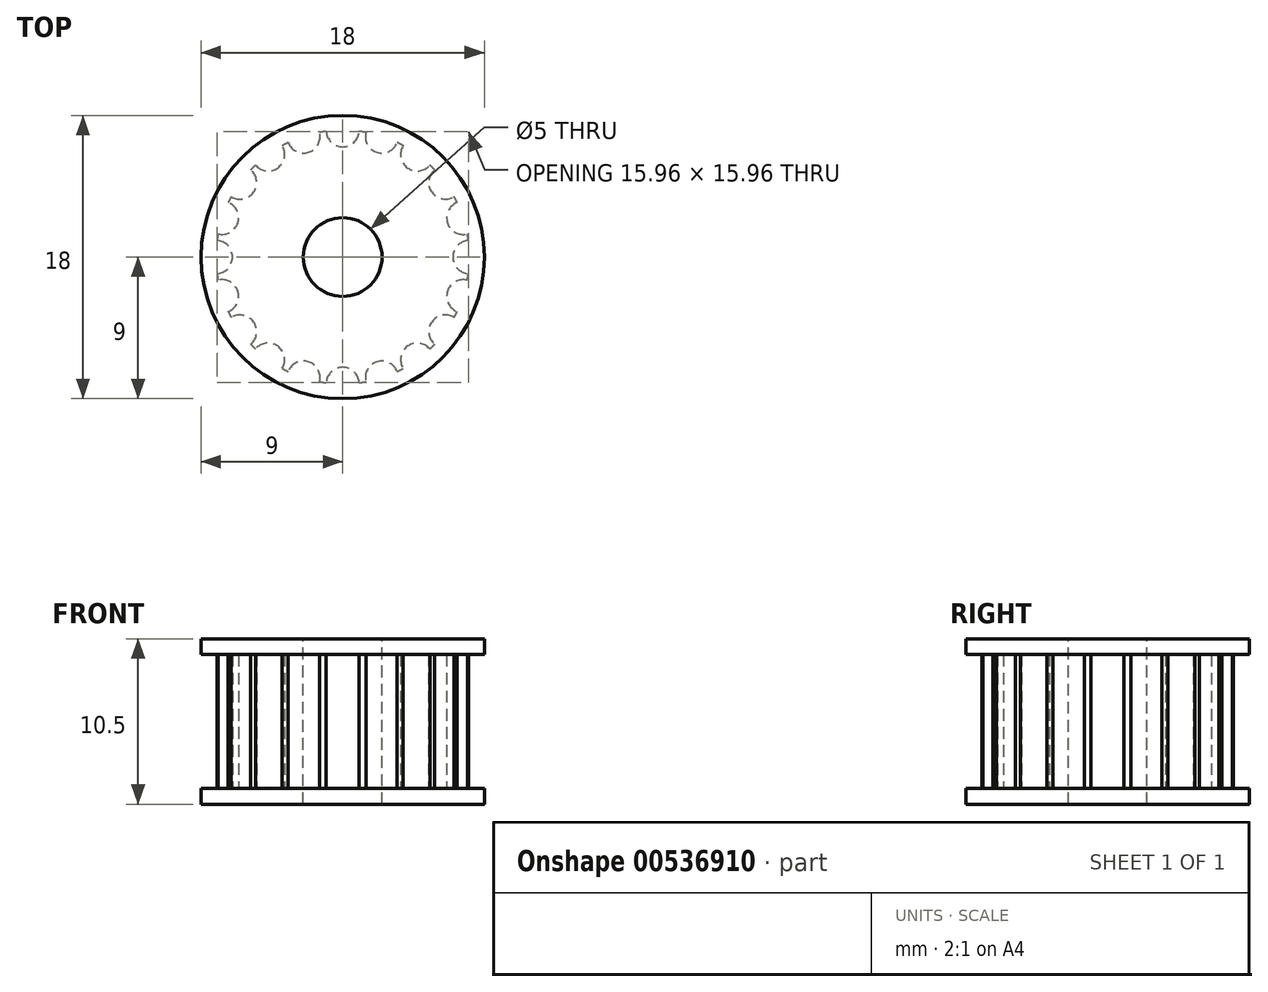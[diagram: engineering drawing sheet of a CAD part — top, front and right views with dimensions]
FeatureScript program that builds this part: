
annotation { "Feature Type Name" : "Feature", "Feature Type Description" : "" }
export const myFeature = defineFeature(function(context is Context, id is Id, definition is map)
    precondition{}
    {
        {
            var Q0;
            Q0=qCreatedBy(makeId("Front.planeOp"),FACE);
            var sketch = newSketch(context, id + "F0", { "sketchPlane" : qUnion([Q0])});
            skLineSegment(sketch, "E0", {"start": v(0, 14.86) * mm, "end": v(0, -20.88) * mm, "construction": true});
            skLineSegment(sketch, "E1", {"start": v(2.5, 5.25) * mm, "end": v(9, 5.25) * mm});
            skLineSegment(sketch, "E2", {"start": v(9, 5.25) * mm, "end": v(9, 4.25) * mm});
            skLineSegment(sketch, "E3", {"start": v(9, 4.25) * mm, "end": v(7, 4.25) * mm});
            skLineSegment(sketch, "E4", {"start": v(7, 4.25) * mm, "end": v(7, -4.25) * mm});
            skLineSegment(sketch, "E5", {"start": v(7, -4.25) * mm, "end": v(9, -4.25) * mm});
            skLineSegment(sketch, "E6", {"start": v(9, -4.25) * mm, "end": v(9, -5.25) * mm});
            skLineSegment(sketch, "E7", {"start": v(9, -5.25) * mm, "end": v(2.5, -5.25) * mm});
            skLineSegment(sketch, "E8", {"start": v(2.5, 5.25) * mm, "end": v(2.5, -5.25) * mm});
            skLineSegment(sketch, "E9", {"start": v(0, 0) * mm, "end": v(2.5, 0) * mm, "construction": true});
            skSolve(sketch);
        }
        {
            var Q0;
            Q0=makeQuery(id+"F0.imprint","IMPRINT",FACE,{"disambiguationData":[TD([[makeQuery(id+"F0.imprint","IMPRINT",EDGE,{"derivedFrom":sQuery(id+"F0.wireOp",EDGE,"E1")}),-1.0]])]});
            var Q1;
            Q1=sQuery(id+"F0.wireOp",EDGE,"E0");
            revolve(context, id + "F1", {"entities" : qUnion([Q0]), "axis" : qUnion([Q1]), "revolveType" : RevolveType.FULL});
        }
        {
            var Q0;
            Q0=makeQuery(id+"F1.opRevolve","SWEPT_FACE",FACE,{"disambiguationData":[OSD([sQuery(id+"F0.wireOp",EDGE,"E5")])]});
            var sketch = newSketch(context, id + "F2", { "sketchPlane" : qUnion([Q0])});
            skArc(sketch, "E10", {"start": v(-1.05, 7.98) * mm, "mid": v(0, 7) * mm, "end": v(1.05, 7.98) * mm});
            skArc(sketch, "E11.1.0", {"start": v(-3.46, 7.27) * mm, "mid": v(-2.16, 6.66) * mm, "end": v(-1.47, 7.91) * mm});
            skArc(sketch, "E11.2.0", {"start": v(-5.54, 5.84) * mm, "mid": v(-4.11, 5.66) * mm, "end": v(-3.84, 7.07) * mm});
            skArc(sketch, "E11.3.0", {"start": v(-7.07, 3.84) * mm, "mid": v(-5.66, 4.11) * mm, "end": v(-5.84, 5.54) * mm});
            skArc(sketch, "E11.4.0", {"start": v(-7.91, 1.47) * mm, "mid": v(-6.66, 2.16) * mm, "end": v(-7.27, 3.46) * mm});
            skArc(sketch, "E11.5.0", {"start": v(-7.98, -1.05) * mm, "mid": v(-7, 0) * mm, "end": v(-7.98, 1.05) * mm});
            skArc(sketch, "E11.6.0", {"start": v(-7.27, -3.46) * mm, "mid": v(-6.66, -2.16) * mm, "end": v(-7.91, -1.47) * mm});
            skArc(sketch, "E11.7.0", {"start": v(-5.84, -5.54) * mm, "mid": v(-5.66, -4.11) * mm, "end": v(-7.07, -3.84) * mm});
            skArc(sketch, "E11.8.0", {"start": v(-3.84, -7.07) * mm, "mid": v(-4.11, -5.66) * mm, "end": v(-5.54, -5.84) * mm});
            skArc(sketch, "E11.9.0", {"start": v(-1.47, -7.91) * mm, "mid": v(-2.16, -6.66) * mm, "end": v(-3.46, -7.27) * mm});
            skArc(sketch, "E11.10.0", {"start": v(1.05, -7.98) * mm, "mid": v(0, -7) * mm, "end": v(-1.05, -7.98) * mm});
            skArc(sketch, "E11.11.0", {"start": v(3.46, -7.27) * mm, "mid": v(2.16, -6.66) * mm, "end": v(1.47, -7.91) * mm});
            skArc(sketch, "E11.12.0", {"start": v(5.54, -5.84) * mm, "mid": v(4.11, -5.66) * mm, "end": v(3.84, -7.07) * mm});
            skArc(sketch, "E11.13.0", {"start": v(7.07, -3.84) * mm, "mid": v(5.66, -4.11) * mm, "end": v(5.84, -5.54) * mm});
            skArc(sketch, "E11.14.0", {"start": v(7.91, -1.47) * mm, "mid": v(6.66, -2.16) * mm, "end": v(7.27, -3.46) * mm});
            skArc(sketch, "E11.15.0", {"start": v(7.98, 1.05) * mm, "mid": v(7, 0) * mm, "end": v(7.98, -1.05) * mm});
            skArc(sketch, "E11.16.0", {"start": v(7.27, 3.46) * mm, "mid": v(6.66, 2.16) * mm, "end": v(7.91, 1.47) * mm});
            skArc(sketch, "E11.17.0", {"start": v(5.84, 5.54) * mm, "mid": v(5.66, 4.11) * mm, "end": v(7.07, 3.84) * mm});
            skArc(sketch, "E11.18.0", {"start": v(3.84, 7.07) * mm, "mid": v(4.11, 5.66) * mm, "end": v(5.54, 5.84) * mm});
            skArc(sketch, "E11.19.0", {"start": v(1.47, 7.91) * mm, "mid": v(2.16, 6.66) * mm, "end": v(3.46, 7.27) * mm});
            skPoint(sketch, "E11.center", {"position": v(0, 0) * mm});
            skCircle(sketch, "E12", {"center": v(0, 0) * mm, "radius": 8.05 * mm});
            skCircle(sketch, "E13", {"center": v(0, 0) * mm, "radius": 6.5 * mm});
            skSolve(sketch);
        }
        {
            var Q0;
            {var subQ0=sQuery(id+"F2.wireOp",EDGE,"E12");var subQ1=sQuery(id+"F2.wireOp",EDGE,"E11.13.0");var subQ2=makeQuery(id+"F2.imprint","INTERSECT",VERTEX,{"disambiguationData":[OD(0.0)],"derivedFrom":[subQ1,subQ0]});Q0=makeQuery(id+"F2.imprint","IMPRINT",FACE,{"disambiguationData":[TD([[makeQuery(id+"F2.imprint","IMPRINT",EDGE,{"disambiguationData":[TD([[subQ2,-1.0]])],"derivedFrom":subQ0}),1.0]])]});}
            var Q1;
            {var subQ0=sQuery(id+"F2.wireOp",EDGE,"E12");var subQ1=sQuery(id+"F2.wireOp",EDGE,"E11.14.0");var subQ2=makeQuery(id+"F2.imprint","INTERSECT",VERTEX,{"disambiguationData":[OD(0.0)],"derivedFrom":[subQ1,subQ0]});Q1=makeQuery(id+"F2.imprint","IMPRINT",FACE,{"disambiguationData":[TD([[makeQuery(id+"F2.imprint","IMPRINT",EDGE,{"disambiguationData":[TD([[subQ2,-1.0]])],"derivedFrom":subQ0}),1.0]])]});}
            var Q2;
            {var subQ0=sQuery(id+"F2.wireOp",EDGE,"E12");var subQ1=sQuery(id+"F2.wireOp",EDGE,"E11.15.0");var subQ2=makeQuery(id+"F2.imprint","INTERSECT",VERTEX,{"disambiguationData":[OD(0.0)],"derivedFrom":[subQ1,subQ0]});Q2=makeQuery(id+"F2.imprint","IMPRINT",FACE,{"disambiguationData":[TD([[makeQuery(id+"F2.imprint","IMPRINT",EDGE,{"disambiguationData":[TD([[subQ2,-1.0]])],"derivedFrom":subQ0}),1.0]])]});}
            var Q3;
            {var subQ0=sQuery(id+"F2.wireOp",EDGE,"E12");var subQ1=sQuery(id+"F2.wireOp",EDGE,"E11.12.0");var subQ2=makeQuery(id+"F2.imprint","INTERSECT",VERTEX,{"disambiguationData":[OD(0.0)],"derivedFrom":[subQ1,subQ0]});Q3=makeQuery(id+"F2.imprint","IMPRINT",FACE,{"disambiguationData":[TD([[makeQuery(id+"F2.imprint","IMPRINT",EDGE,{"disambiguationData":[TD([[subQ2,-1.0]])],"derivedFrom":subQ0}),1.0]])]});}
            var Q4;
            {var subQ0=sQuery(id+"F2.wireOp",EDGE,"E12");var subQ1=sQuery(id+"F2.wireOp",EDGE,"E11.11.0");var subQ2=makeQuery(id+"F2.imprint","INTERSECT",VERTEX,{"disambiguationData":[OD(0.0)],"derivedFrom":[subQ1,subQ0]});Q4=makeQuery(id+"F2.imprint","IMPRINT",FACE,{"disambiguationData":[TD([[makeQuery(id+"F2.imprint","IMPRINT",EDGE,{"disambiguationData":[TD([[subQ2,-1.0]])],"derivedFrom":subQ0}),1.0]])]});}
            var Q5;
            {var subQ0=sQuery(id+"F2.wireOp",EDGE,"E12");var subQ1=sQuery(id+"F2.wireOp",EDGE,"E11.10.0");var subQ2=makeQuery(id+"F2.imprint","INTERSECT",VERTEX,{"disambiguationData":[OD(0.0)],"derivedFrom":[subQ1,subQ0]});Q5=makeQuery(id+"F2.imprint","IMPRINT",FACE,{"disambiguationData":[TD([[makeQuery(id+"F2.imprint","IMPRINT",EDGE,{"disambiguationData":[TD([[subQ2,-1.0]])],"derivedFrom":subQ0}),1.0]])]});}
            var Q6;
            {var subQ0=sQuery(id+"F2.wireOp",EDGE,"E12");var subQ1=sQuery(id+"F2.wireOp",EDGE,"E11.9.0");var subQ2=makeQuery(id+"F2.imprint","INTERSECT",VERTEX,{"disambiguationData":[OD(0.0)],"derivedFrom":[subQ1,subQ0]});Q6=makeQuery(id+"F2.imprint","IMPRINT",FACE,{"disambiguationData":[TD([[makeQuery(id+"F2.imprint","IMPRINT",EDGE,{"disambiguationData":[TD([[subQ2,-1.0]])],"derivedFrom":subQ0}),1.0]])]});}
            var Q7;
            {var subQ0=sQuery(id+"F2.wireOp",EDGE,"E12");var subQ1=sQuery(id+"F2.wireOp",EDGE,"E11.8.0");var subQ2=makeQuery(id+"F2.imprint","INTERSECT",VERTEX,{"disambiguationData":[OD(0.0)],"derivedFrom":[subQ1,subQ0]});Q7=makeQuery(id+"F2.imprint","IMPRINT",FACE,{"disambiguationData":[TD([[makeQuery(id+"F2.imprint","IMPRINT",EDGE,{"disambiguationData":[TD([[subQ2,-1.0]])],"derivedFrom":subQ0}),1.0]])]});}
            var Q8;
            {var subQ0=sQuery(id+"F2.wireOp",EDGE,"E12");var subQ1=sQuery(id+"F2.wireOp",EDGE,"E11.7.0");var subQ2=makeQuery(id+"F2.imprint","INTERSECT",VERTEX,{"disambiguationData":[OD(0.0)],"derivedFrom":[subQ1,subQ0]});Q8=makeQuery(id+"F2.imprint","IMPRINT",FACE,{"disambiguationData":[TD([[makeQuery(id+"F2.imprint","IMPRINT",EDGE,{"disambiguationData":[TD([[subQ2,-1.0]])],"derivedFrom":subQ0}),1.0]])]});}
            var Q9;
            {var subQ0=sQuery(id+"F2.wireOp",EDGE,"E12");var subQ1=sQuery(id+"F2.wireOp",EDGE,"E11.6.0");var subQ2=makeQuery(id+"F2.imprint","INTERSECT",VERTEX,{"disambiguationData":[OD(0.0)],"derivedFrom":[subQ1,subQ0]});Q9=makeQuery(id+"F2.imprint","IMPRINT",FACE,{"disambiguationData":[TD([[makeQuery(id+"F2.imprint","IMPRINT",EDGE,{"disambiguationData":[TD([[subQ2,-1.0]])],"derivedFrom":subQ0}),1.0]])]});}
            var Q10;
            {var subQ0=sQuery(id+"F2.wireOp",EDGE,"E12");var subQ1=sQuery(id+"F2.wireOp",EDGE,"E11.5.0");var subQ2=makeQuery(id+"F2.imprint","INTERSECT",VERTEX,{"disambiguationData":[OD(0.0)],"derivedFrom":[subQ1,subQ0]});Q10=makeQuery(id+"F2.imprint","IMPRINT",FACE,{"disambiguationData":[TD([[makeQuery(id+"F2.imprint","IMPRINT",EDGE,{"disambiguationData":[TD([[subQ2,-1.0]])],"derivedFrom":subQ0}),1.0]])]});}
            var Q11;
            {var subQ0=sQuery(id+"F2.wireOp",EDGE,"E12");var subQ1=sQuery(id+"F2.wireOp",EDGE,"E11.4.0");var subQ2=makeQuery(id+"F2.imprint","INTERSECT",VERTEX,{"disambiguationData":[OD(0.0)],"derivedFrom":[subQ1,subQ0]});Q11=makeQuery(id+"F2.imprint","IMPRINT",FACE,{"disambiguationData":[TD([[makeQuery(id+"F2.imprint","IMPRINT",EDGE,{"disambiguationData":[TD([[subQ2,-1.0]])],"derivedFrom":subQ0}),1.0]])]});}
            var Q12;
            {var subQ0=sQuery(id+"F2.wireOp",EDGE,"E12");var subQ1=sQuery(id+"F2.wireOp",EDGE,"E11.3.0");var subQ2=makeQuery(id+"F2.imprint","INTERSECT",VERTEX,{"disambiguationData":[OD(0.0)],"derivedFrom":[subQ1,subQ0]});Q12=makeQuery(id+"F2.imprint","IMPRINT",FACE,{"disambiguationData":[TD([[makeQuery(id+"F2.imprint","IMPRINT",EDGE,{"disambiguationData":[TD([[subQ2,-1.0]])],"derivedFrom":subQ0}),1.0]])]});}
            var Q13;
            {var subQ0=sQuery(id+"F2.wireOp",EDGE,"E12");var subQ1=sQuery(id+"F2.wireOp",EDGE,"E11.2.0");var subQ2=makeQuery(id+"F2.imprint","INTERSECT",VERTEX,{"disambiguationData":[OD(0.0)],"derivedFrom":[subQ1,subQ0]});Q13=makeQuery(id+"F2.imprint","IMPRINT",FACE,{"disambiguationData":[TD([[makeQuery(id+"F2.imprint","IMPRINT",EDGE,{"disambiguationData":[TD([[subQ2,-1.0]])],"derivedFrom":subQ0}),1.0]])]});}
            var Q14;
            {var subQ0=sQuery(id+"F2.wireOp",EDGE,"E12");var subQ1=sQuery(id+"F2.wireOp",EDGE,"E11.1.0");var subQ2=makeQuery(id+"F2.imprint","INTERSECT",VERTEX,{"disambiguationData":[OD(0.0)],"derivedFrom":[subQ1,subQ0]});Q14=makeQuery(id+"F2.imprint","IMPRINT",FACE,{"disambiguationData":[TD([[makeQuery(id+"F2.imprint","IMPRINT",EDGE,{"disambiguationData":[TD([[subQ2,-1.0]])],"derivedFrom":subQ0}),1.0]])]});}
            var Q15;
            {var subQ0=sQuery(id+"F2.wireOp",EDGE,"E12");var subQ1=sQuery(id+"F2.wireOp",EDGE,"E10");var subQ2=makeQuery(id+"F2.imprint","INTERSECT",VERTEX,{"disambiguationData":[OD(0.0)],"derivedFrom":[subQ1,subQ0]});Q15=makeQuery(id+"F2.imprint","IMPRINT",FACE,{"disambiguationData":[TD([[makeQuery(id+"F2.imprint","IMPRINT",EDGE,{"disambiguationData":[TD([[subQ2,-1.0]])],"derivedFrom":subQ0}),1.0]])]});}
            var Q16;
            {var subQ0=sQuery(id+"F2.wireOp",EDGE,"E12");var subQ1=sQuery(id+"F2.wireOp",EDGE,"E10");var subQ2=makeQuery(id+"F2.imprint","INTERSECT",VERTEX,{"disambiguationData":[OD(1.0)],"derivedFrom":[subQ1,subQ0]});Q16=makeQuery(id+"F2.imprint","IMPRINT",FACE,{"disambiguationData":[TD([[makeQuery(id+"F2.imprint","IMPRINT",EDGE,{"disambiguationData":[TD([[subQ2,1.0]])],"derivedFrom":subQ0}),1.0]])]});}
            var Q17;
            {var subQ0=sQuery(id+"F2.wireOp",EDGE,"E12");var subQ1=sQuery(id+"F2.wireOp",EDGE,"E11.18.0");var subQ2=makeQuery(id+"F2.imprint","INTERSECT",VERTEX,{"disambiguationData":[OD(0.0)],"derivedFrom":[subQ1,subQ0]});Q17=makeQuery(id+"F2.imprint","IMPRINT",FACE,{"disambiguationData":[TD([[makeQuery(id+"F2.imprint","IMPRINT",EDGE,{"disambiguationData":[TD([[subQ2,-1.0]])],"derivedFrom":subQ0}),1.0]])]});}
            var Q18;
            {var subQ0=sQuery(id+"F2.wireOp",EDGE,"E12");var subQ1=sQuery(id+"F2.wireOp",EDGE,"E11.17.0");var subQ2=makeQuery(id+"F2.imprint","INTERSECT",VERTEX,{"disambiguationData":[OD(0.0)],"derivedFrom":[subQ1,subQ0]});Q18=makeQuery(id+"F2.imprint","IMPRINT",FACE,{"disambiguationData":[TD([[makeQuery(id+"F2.imprint","IMPRINT",EDGE,{"disambiguationData":[TD([[subQ2,-1.0]])],"derivedFrom":subQ0}),1.0]])]});}
            var Q19;
            {var subQ0=sQuery(id+"F2.wireOp",EDGE,"E12");var subQ1=sQuery(id+"F2.wireOp",EDGE,"E11.16.0");var subQ2=makeQuery(id+"F2.imprint","INTERSECT",VERTEX,{"disambiguationData":[OD(0.0)],"derivedFrom":[subQ1,subQ0]});Q19=makeQuery(id+"F2.imprint","IMPRINT",FACE,{"disambiguationData":[TD([[makeQuery(id+"F2.imprint","IMPRINT",EDGE,{"disambiguationData":[TD([[subQ2,-1.0]])],"derivedFrom":subQ0}),1.0]])]});}
            extrude(context, id + "F3", {"entities" : qUnion([Q0, Q1, Q2, Q3, Q4, Q5, Q6, Q7, Q8, Q9, Q10, Q11, Q12, Q13, Q14, Q15, Q16, Q17, Q18, Q19]), "operationType" : NewBodyOperationType.ADD, "depth" : 8.5 * mm, "offsetDistance" : 25 * mm});
        }
    });
